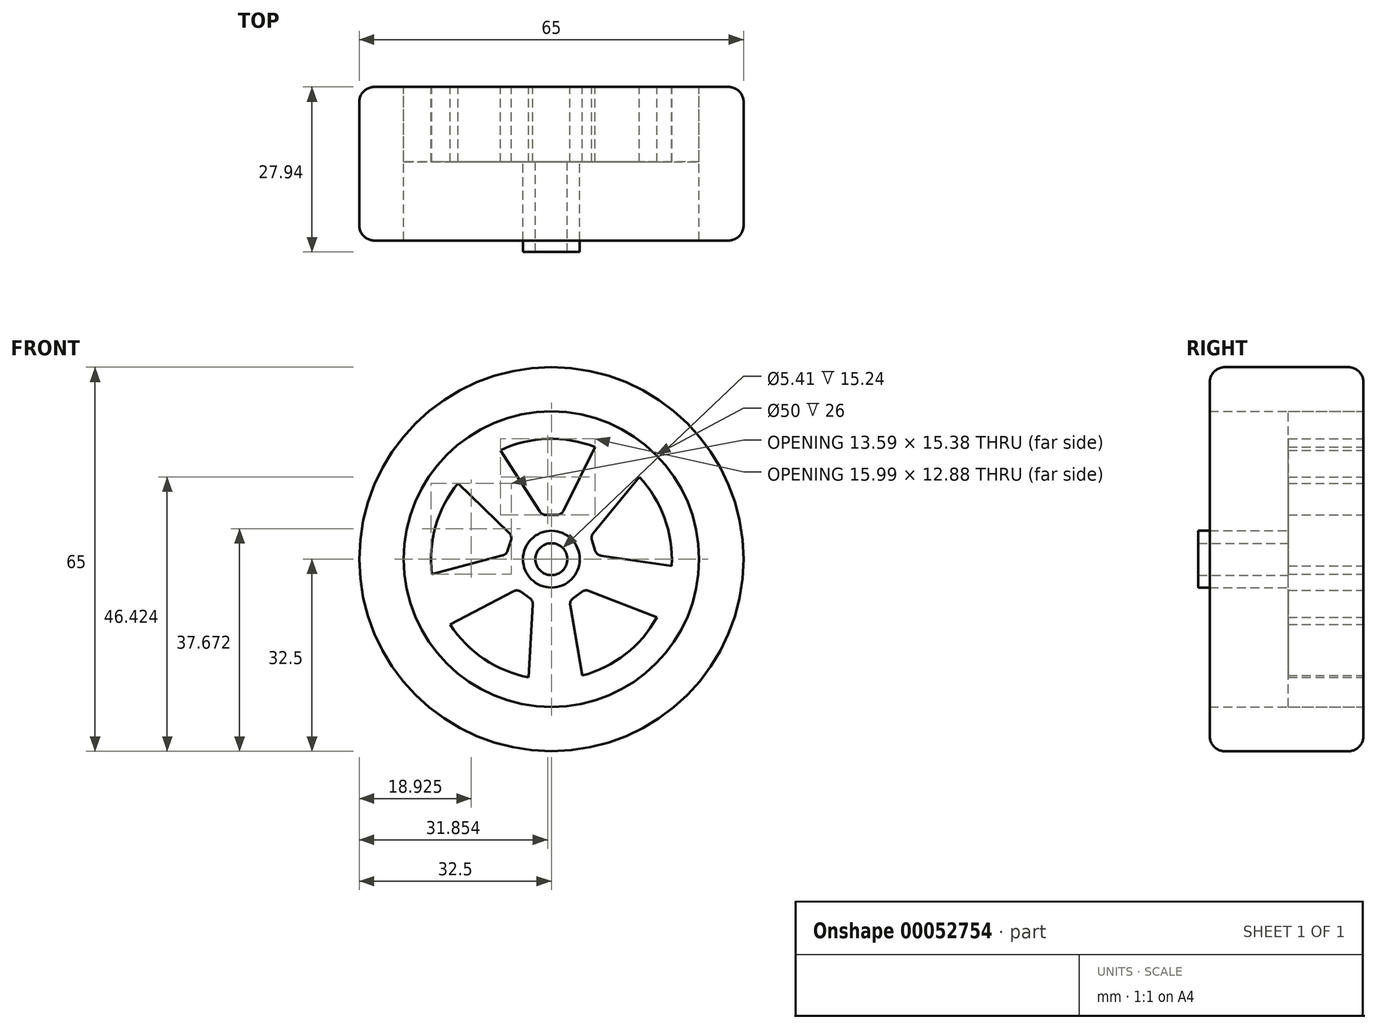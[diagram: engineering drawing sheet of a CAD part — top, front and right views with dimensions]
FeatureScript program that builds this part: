
annotation { "Feature Type Name" : "Feature", "Feature Type Description" : "" }
export const myFeature = defineFeature(function(context is Context, id is Id, definition is map)
    precondition{}
    {
        {
            var Q0;
            Q0=qCreatedBy(makeId("Front.planeOp"),FACE);
            var sketch = newSketch(context, id + "F0", { "sketchPlane" : qUnion([Q0])});
            skCircle(sketch, "E0", {"center": v(0, 0) * mm, "radius": 32.5 * mm});
            skCircle(sketch, "E1", {"center": v(0, 0) * mm, "radius": 25 * mm});
            skSolve(sketch);
        }
        {
            var Q0;
            Q0=makeQuery(id+"F0.imprint","IMPRINT",FACE,{"disambiguationData":[TD([[makeQuery(id+"F0.imprint","IMPRINT",EDGE,{"derivedFrom":sQuery(id+"F0.wireOp",EDGE,"E0")}),1.0]])]});
            extrude(context, id + "F1", {"entities" : qUnion([Q0]), "depth" : 26 * mm});
        }
        {
            var Q0;
            Q0=qCreatedBy(makeId("Front.planeOp"),FACE);
            var sketch = newSketch(context, id + "F2", { "sketchPlane" : qUnion([Q0])});
            skCircle(sketch, "E2.0", {"center": v(0, 0) * mm, "radius": 25 * mm});
            skArc(sketch, "E3", {"start": v(-15.8, 12.86) * mm, "mid": v(-19.58, 5.62) * mm, "end": v(-20.22, -2.52) * mm});
            skLineSegment(sketch, "E4", {"start": v(-8.64, 18.45) * mm, "end": v(-1.97, 8.07) * mm});
            skLineSegment(sketch, "E5", {"start": v(-0.9, 7.49) * mm, "end": v(0.9, 7.49) * mm});
            skLineSegment(sketch, "E6", {"start": v(2.03, 8.2) * mm, "end": v(7.35, 19) * mm});
            skPoint(sketch, "E7.visualSharp", {"position": v(-1.6, 7.49) * mm});
            skArc(sketch, "E7.filletArc", {"start": v(-1.97, 8.07) * mm, "mid": v(-1.51, 7.64) * mm, "end": v(-0.9, 7.49) * mm});
            skPoint(sketch, "E8.visualSharp", {"position": v(1.69, 7.49) * mm});
            skArc(sketch, "E8.filletArc", {"start": v(0.9, 7.49) * mm, "mid": v(1.57, 7.68) * mm, "end": v(2.03, 8.2) * mm});
            skPoint(sketch, "E9.1.0", {"position": v(-6.6, 3.92) * mm});
            skPoint(sketch, "E9.1.1", {"position": v(-7.61, 0.8) * mm});
            skLineSegment(sketch, "E9.1.2", {"start": v(-20.22, -2.52) * mm, "end": v(-8.28, 0.62) * mm});
            skLineSegment(sketch, "E9.1.3", {"start": v(-7.4, 1.45) * mm, "end": v(-6.84, 3.16) * mm});
            skLineSegment(sketch, "E9.1.4", {"start": v(-7.17, 4.47) * mm, "end": v(-15.8, 12.86) * mm});
            skArc(sketch, "E9.1.5", {"start": v(-8.28, 0.62) * mm, "mid": v(-7.73, 0.92) * mm, "end": v(-7.4, 1.45) * mm});
            skArc(sketch, "E9.1.6", {"start": v(-6.84, 3.16) * mm, "mid": v(-6.82, 3.86) * mm, "end": v(-7.17, 4.47) * mm});
            skPoint(sketch, "E9.2.0", {"position": v(-5.76, -5.07) * mm});
            skPoint(sketch, "E9.2.1", {"position": v(-3.1, -7) * mm});
            skLineSegment(sketch, "E9.2.2", {"start": v(-3.85, -20) * mm, "end": v(-3.15, -7.69) * mm});
            skLineSegment(sketch, "E9.2.3", {"start": v(-3.67, -6.59) * mm, "end": v(-5.12, -5.53) * mm});
            skLineSegment(sketch, "E9.2.4", {"start": v(-6.46, -5.43) * mm, "end": v(-17.12, -11.05) * mm});
            skArc(sketch, "E9.2.5", {"start": v(-3.15, -7.69) * mm, "mid": v(-3.27, -7.07) * mm, "end": v(-3.67, -6.59) * mm});
            skArc(sketch, "E9.2.6", {"start": v(-5.12, -5.53) * mm, "mid": v(-5.78, -5.3) * mm, "end": v(-6.46, -5.43) * mm});
            skPoint(sketch, "E9.3.0", {"position": v(3.04, -7.05) * mm});
            skPoint(sketch, "E9.3.1", {"position": v(5.7, -5.12) * mm});
            skLineSegment(sketch, "E9.3.2", {"start": v(17.84, -9.85) * mm, "end": v(6.34, -5.37) * mm});
            skLineSegment(sketch, "E9.3.3", {"start": v(5.13, -5.53) * mm, "end": v(3.68, -6.58) * mm});
            skLineSegment(sketch, "E9.3.4", {"start": v(3.17, -7.83) * mm, "end": v(5.22, -19.7) * mm});
            skArc(sketch, "E9.3.5", {"start": v(6.34, -5.37) * mm, "mid": v(5.71, -5.3) * mm, "end": v(5.13, -5.53) * mm});
            skArc(sketch, "E9.3.6", {"start": v(3.68, -6.58) * mm, "mid": v(3.25, -7.13) * mm, "end": v(3.17, -7.83) * mm});
            skPoint(sketch, "E9.4.0", {"position": v(7.64, 0.71) * mm});
            skPoint(sketch, "E9.4.1", {"position": v(6.63, 3.83) * mm});
            skLineSegment(sketch, "E9.4.2", {"start": v(14.88, 13.92) * mm, "end": v(7.07, 4.37) * mm});
            skLineSegment(sketch, "E9.4.3", {"start": v(6.84, 3.17) * mm, "end": v(7.4, 1.46) * mm});
            skLineSegment(sketch, "E9.4.4", {"start": v(8.42, 0.6) * mm, "end": v(20.34, -1.12) * mm});
            skArc(sketch, "E9.4.5", {"start": v(7.07, 4.37) * mm, "mid": v(6.8, 3.8) * mm, "end": v(6.84, 3.17) * mm});
            skArc(sketch, "E9.4.6", {"start": v(7.4, 1.46) * mm, "mid": v(7.79, 0.88) * mm, "end": v(8.42, 0.6) * mm});
            skArc(sketch, "E10.trimOffspring", {"start": v(7.35, 19) * mm, "mid": v(-0.7, 20.36) * mm, "end": v(-8.64, 18.45) * mm});
            skArc(sketch, "E11.trimOffspring", {"start": v(20.34, -1.12) * mm, "mid": v(19.15, 6.96) * mm, "end": v(14.88, 13.92) * mm});
            skArc(sketch, "E12.trimOffspring", {"start": v(5.22, -19.7) * mm, "mid": v(12.54, -16.06) * mm, "end": v(17.84, -9.85) * mm});
            skArc(sketch, "E13.trimOffspring", {"start": v(-17.12, -11.05) * mm, "mid": v(-11.4, -16.89) * mm, "end": v(-3.85, -20) * mm});
            skSolve(sketch);
        }
        {
            var Q0;
            Q0 = qSketchRegion(id + "F2", true);
            extrude(context, id + "F3", {"entities" : qUnion([Q0]), "depth" : 12.7 * mm});
        }
        {
            var Q0;
            Q0=makeQuery(id+"F3.opExtrude","CAP_FACE",FACE,{"disambiguationData":[OSD([sQuery(id+"F2.wireOp",EDGE,"E2.0"),sQuery(id+"F2.wireOp",EDGE,"E3"),sQuery(id+"F2.wireOp",EDGE,"E4"),sQuery(id+"F2.wireOp",EDGE,"E5"),sQuery(id+"F2.wireOp",EDGE,"E6"),sQuery(id+"F2.wireOp",EDGE,"E7.filletArc"),sQuery(id+"F2.wireOp",EDGE,"E8.filletArc"),sQuery(id+"F2.wireOp",EDGE,"E9.1.2"),sQuery(id+"F2.wireOp",EDGE,"E9.1.3"),sQuery(id+"F2.wireOp",EDGE,"E9.1.4"),sQuery(id+"F2.wireOp",EDGE,"E9.1.5"),sQuery(id+"F2.wireOp",EDGE,"E9.1.6"),sQuery(id+"F2.wireOp",EDGE,"E9.2.2"),sQuery(id+"F2.wireOp",EDGE,"E9.2.3"),sQuery(id+"F2.wireOp",EDGE,"E9.2.4"),sQuery(id+"F2.wireOp",EDGE,"E9.2.5"),sQuery(id+"F2.wireOp",EDGE,"E9.2.6"),sQuery(id+"F2.wireOp",EDGE,"E9.3.2"),sQuery(id+"F2.wireOp",EDGE,"E9.3.3"),sQuery(id+"F2.wireOp",EDGE,"E9.3.4"),sQuery(id+"F2.wireOp",EDGE,"E9.3.5"),sQuery(id+"F2.wireOp",EDGE,"E9.3.6"),sQuery(id+"F2.wireOp",EDGE,"E9.4.2"),sQuery(id+"F2.wireOp",EDGE,"E9.4.3"),sQuery(id+"F2.wireOp",EDGE,"E9.4.4"),sQuery(id+"F2.wireOp",EDGE,"E9.4.5"),sQuery(id+"F2.wireOp",EDGE,"E9.4.6"),sQuery(id+"F2.wireOp",EDGE,"E10.trimOffspring"),sQuery(id+"F2.wireOp",EDGE,"E11.trimOffspring"),sQuery(id+"F2.wireOp",EDGE,"E12.trimOffspring"),sQuery(id+"F2.wireOp",EDGE,"E13.trimOffspring")])],"isStart":false});
            var sketch = newSketch(context, id + "F4", { "sketchPlane" : qUnion([Q0])});
            skCircle(sketch, "E14", {"center": v(0, 0) * mm, "radius": 4.8 * mm});
            skCircle(sketch, "E15", {"center": v(0, 0) * mm, "radius": 2.7 * mm});
            skSolve(sketch);
        }
        {
            var Q0;
            Q0 = qSketchRegion(id + "F4", true);
            extrude(context, id + "F5", {"entities" : qUnion([Q0]), "operationType" : NewBodyOperationType.ADD, "depth" : 15.24 * mm});
        }
        {
            var Q0;
            Q0=makeQuery(id+"F1.opExtrude","CAP_EDGE",EDGE,{"disambiguationData":[OSD([sQuery(id+"F0.wireOp",EDGE,"E0")])],"isStart":false});
            var Q1;
            Q1=makeQuery(id+"F1.opExtrude","CAP_EDGE",EDGE,{"disambiguationData":[OSD([sQuery(id+"F0.wireOp",EDGE,"E0")])],"isStart":true});
            fillet(context, id + "F6", {"entities" : qUnion([Q0, Q1]), "radius" : 2.54 * mm, "tangentPropagation" : true, "allowEdgeOverflow" : false});
        }
    });
